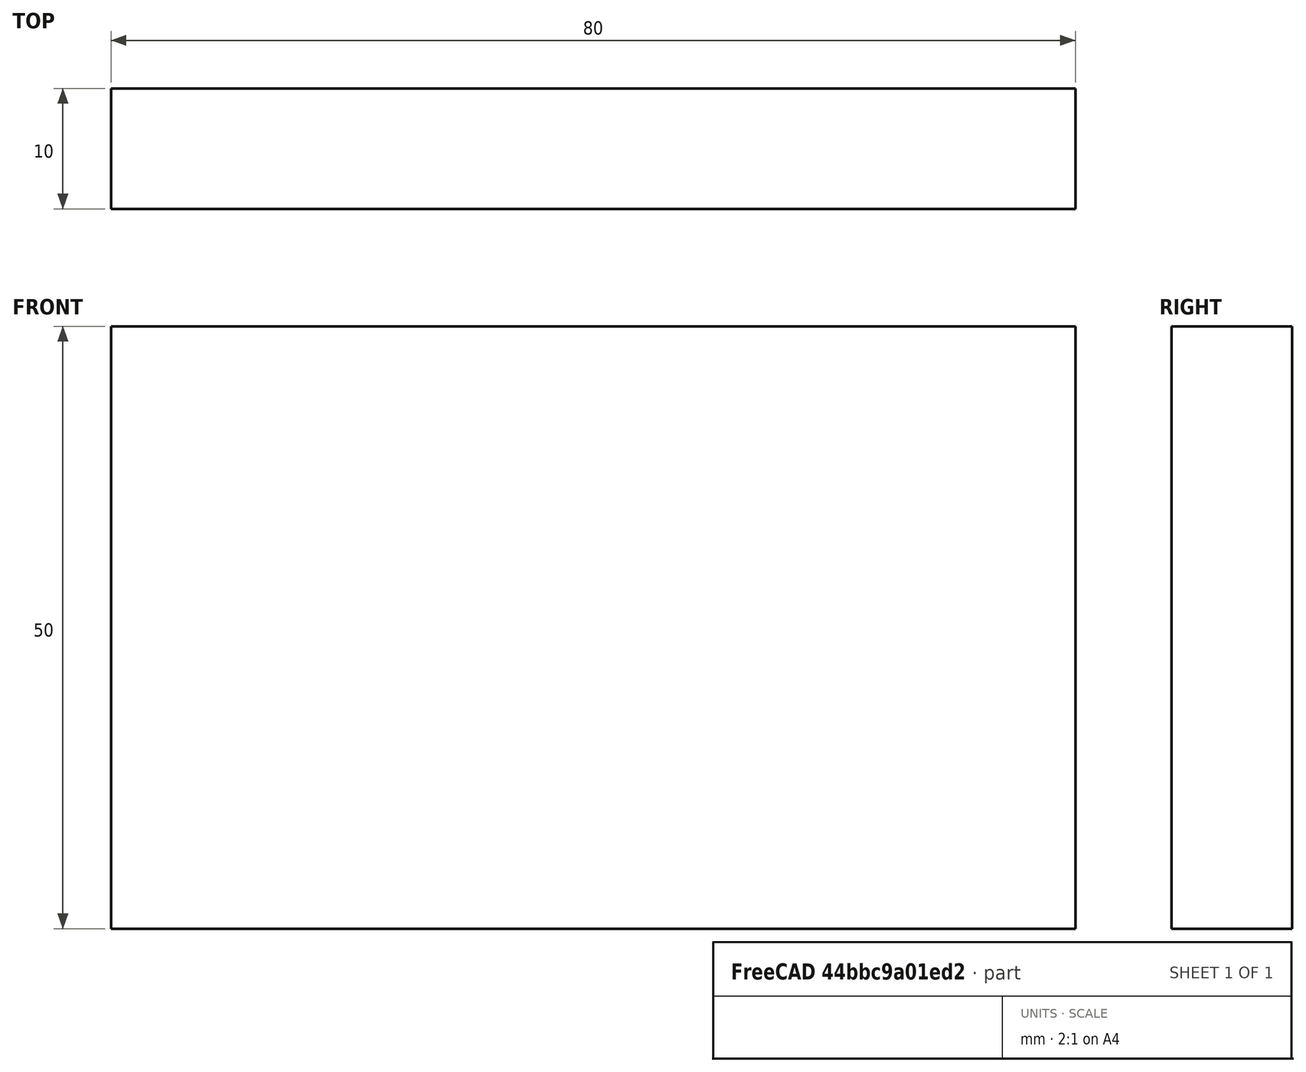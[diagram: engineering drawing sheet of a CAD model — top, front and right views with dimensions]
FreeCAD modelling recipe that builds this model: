
FCSTD DOCUMENT  (FreeCAD 0.15R4671 (Git))
Label: Flat Bar 80x10 EN10058 S235JR
License: All rights reserved
LicenseURL: http://en.wikipedia.org/wiki/All_rights_reserved
objects: Sketcher::SketchObject×1, Part::Extrusion×1
note: 2 computed .brp shape members not serialized (recipe doc carries the construction recipe); baked Part::Feature solids carry a one-line shape summary decoded from their .brp

FEATURE [Sketcher::SketchObject] Sketch
  sketch-geometry (4):
    g0: LineSegment StartX=-40 StartY=-5 StartZ=0 EndX=40 EndY=-5 EndZ=0
    g1: LineSegment StartX=40 StartY=-5 StartZ=0 EndX=40 EndY=5 EndZ=0
    g2: LineSegment StartX=40 StartY=5 StartZ=0 EndX=-40 EndY=5 EndZ=0
    g3: LineSegment StartX=-40 StartY=5 StartZ=0 EndX=-40 EndY=-5 EndZ=0
  constraints (12):
    c: Coincident(g0,g1)
    c: Coincident(g1,g2)
    c: Coincident(g2,g3)
    c: Coincident(g3,g0)
    c: Horizontal(g0)
    c: Horizontal(g2)
    c: Vertical(g1)
    c: Vertical(g3)
    c: Symmetric(g1,g2,g-2)
    c: Symmetric(g0,g1,g-1)
    c: DistanceY(g1) = 10
    c: DistanceX(g0) = 80
FEATURE [Part::Extrusion] Extrude  label="Flat Bar 80x10 EN10058 S235JR"
  Base = -> Sketch
  Dir = (0,0,50)
  Solid = true
